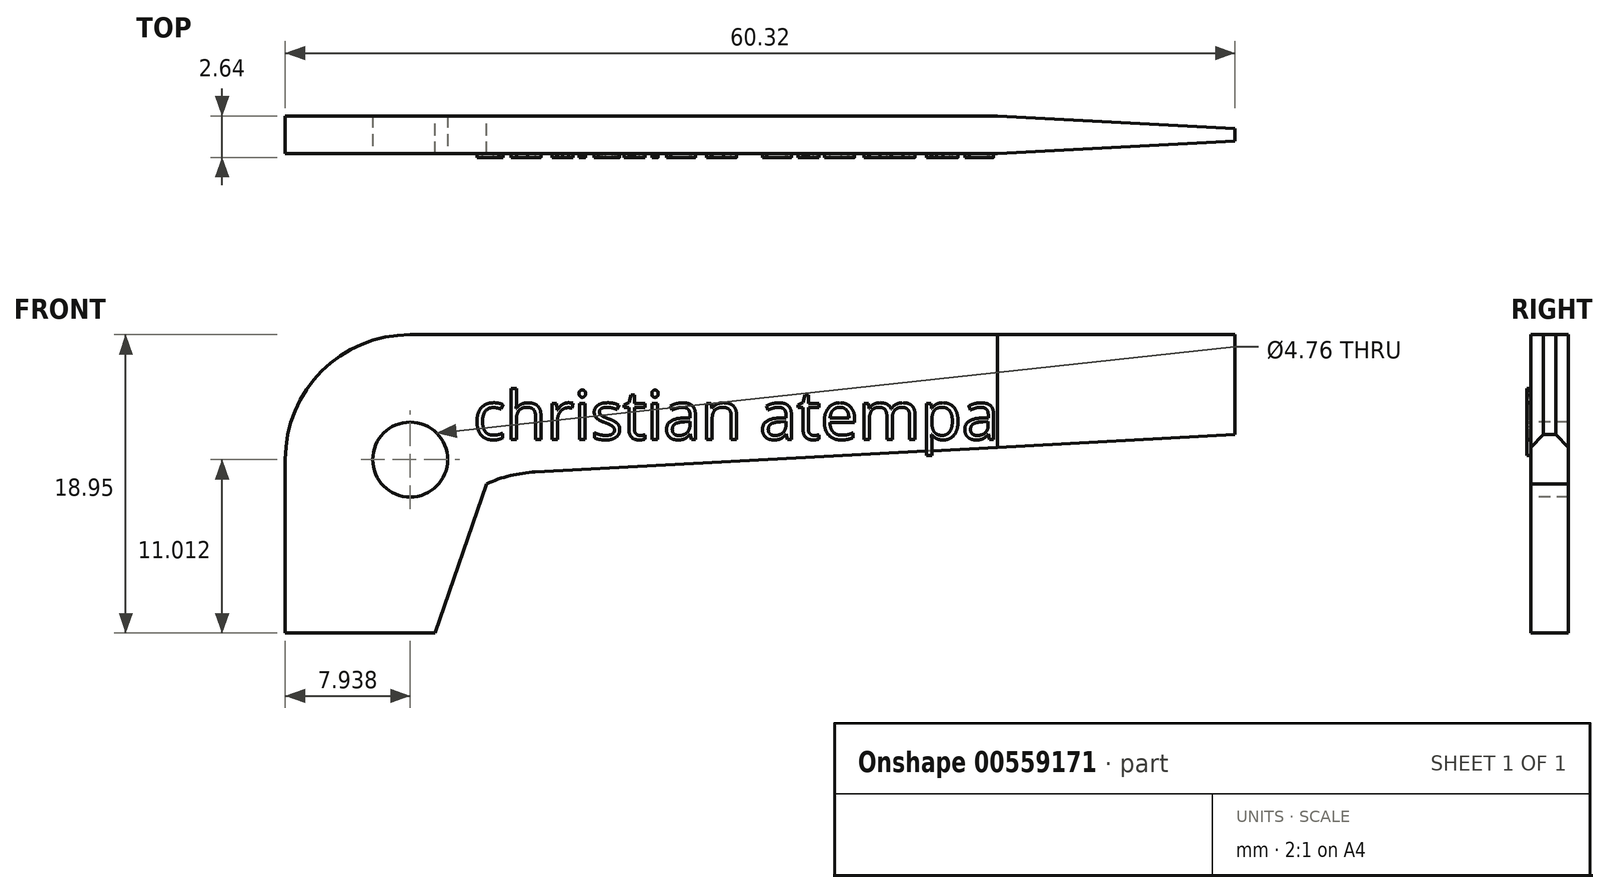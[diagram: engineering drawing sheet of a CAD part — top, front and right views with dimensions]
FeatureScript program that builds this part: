
annotation { "Feature Type Name" : "Feature", "Feature Type Description" : "" }
export const myFeature = defineFeature(function(context is Context, id is Id, definition is map)
    precondition{}
    {
        {
            var Q0;
            Q0=qCreatedBy(makeId("Front.planeOp"),FACE);
            var sketch = newSketch(context, id + "F0", { "sketchPlane" : qUnion([Q0])});
            skLineSegment(sketch, "E0.top", {"start": v(7.94, 18.95) * mm, "end": v(60.33, 18.95) * mm});
            skLineSegment(sketch, "E0.left", {"start": v(0, 0) * mm, "end": v(0, 11.01) * mm});
            skLineSegment(sketch, "E1", {"start": v(9.53, 0) * mm, "end": v(12.79, 9.47) * mm});
            skPoint(sketch, "E1.endSnap0", {"position": v(0, 9.47) * mm});
            skLineSegment(sketch, "E2", {"start": v(60.33, 12.6) * mm, "end": v(15.88, 10.22) * mm});
            skLineSegment(sketch, "E3", {"start": v(0, 0) * mm, "end": v(9.53, 0) * mm});
            skLineSegment(sketch, "E4", {"start": v(60.33, 18.95) * mm, "end": v(60.33, 12.6) * mm});
            skArc(sketch, "E5", {"start": v(15.88, 10.22) * mm, "mid": v(14.3, 10) * mm, "end": v(12.79, 9.47) * mm});
            skPoint(sketch, "E6.visualSharp", {"position": v(0, 18.95) * mm});
            skArc(sketch, "E6.filletArc", {"start": v(7.94, 18.95) * mm, "mid": v(2.32, 16.62) * mm, "end": v(0, 11.01) * mm});
            skSolve(sketch);
        }
        {
            var Q0;
            Q0 = qSketchRegion(id + "F0", true);
            extrude(context, id + "F1", {"entities" : qUnion([Q0]), "depth" : 2.38 * mm, "offsetDistance" : 25.4 * mm});
        }
        {
            var Q0;
            Q0=makeQuery(id+"F1.opExtrude","CAP_FACE",FACE,{"disambiguationData":[OSD([sQuery(id+"F0.wireOp",EDGE,"E0.top"),sQuery(id+"F0.wireOp",EDGE,"E0.left"),sQuery(id+"F0.wireOp",EDGE,"E1"),sQuery(id+"F0.wireOp",EDGE,"E2"),sQuery(id+"F0.wireOp",EDGE,"E3"),sQuery(id+"F0.wireOp",EDGE,"E4"),sQuery(id+"F0.wireOp",EDGE,"E5"),sQuery(id+"F0.wireOp",EDGE,"E6.filletArc")])],"isStart":false});
            var sketch = newSketch(context, id + "F2", { "sketchPlane" : qUnion([Q0])});
            skCircle(sketch, "E7", {"center": v(7.94, 11.01) * mm, "radius": 2.38 * mm});
            skSolve(sketch);
        }
        {
            var Q0;
            Q0=makeQuery(id+"F2.imprint","IMPRINT",FACE,{"disambiguationData":[TD([[makeQuery(id+"F2.imprint","IMPRINT",EDGE,{"derivedFrom":sQuery(id+"F2.wireOp",EDGE,"E7")}),1.0]])]});
            extrude(context, id + "F3", {"entities" : qUnion([Q0]), "operationType" : NewBodyOperationType.REMOVE, "endBound" : BoundingType.THROUGH_ALL, "oppositeDirection" : true, "depth" : 25.4 * mm, "offsetDistance" : 25.4 * mm});
        }
        {
            var Q0;
            Q0=makeQuery(id+"F1.opExtrude","SWEPT_FACE",FACE,{"disambiguationData":[OSD([sQuery(id+"F0.wireOp",EDGE,"E0.top")])]});
            var sketch = newSketch(context, id + "F4", { "sketchPlane" : qUnion([Q0])});
            skLineSegment(sketch, "E8", {"start": v(45.24, 0) * mm, "end": v(60.33, -0.8) * mm});
            skLineSegment(sketch, "E9", {"start": v(60.33, 0) * mm, "end": v(45.24, 0) * mm});
            skLineSegment(sketch, "E10.MirrorCS", {"start": v(45.24, -2.38) * mm, "end": v(60.33, -1.59) * mm});
            skLineSegment(sketch, "E11.MirrorCS", {"start": v(60.33, -2.38) * mm, "end": v(45.24, -2.38) * mm});
            skSolve(sketch);
        }
        {
            var Q0;
            {var subQ0=sQuery(id+"F4.wireOp",EDGE,"E10.MirrorCS");Q0=makeQuery(id+"F4.imprint","IMPRINT",FACE,{"disambiguationData":[TD([[makeQuery(id+"F4.imprint","IMPRINT",EDGE,{"derivedFrom":subQ0}),-1.0]])]});}
            var Q1;
            {var subQ0=sQuery(id+"F4.wireOp",EDGE,"E8");Q1=makeQuery(id+"F4.imprint","IMPRINT",FACE,{"disambiguationData":[TD([[makeQuery(id+"F4.imprint","IMPRINT",EDGE,{"derivedFrom":subQ0}),1.0]])]});}
            extrude(context, id + "F5", {"entities" : qUnion([Q0, Q1]), "operationType" : NewBodyOperationType.REMOVE, "oppositeDirection" : true, "depth" : 25.4 * mm, "offsetDistance" : 25.4 * mm});
        }
        {
            var Q0;
            Q0=makeQuery(id+"F1.opExtrude","CAP_FACE",FACE,{"disambiguationData":[OSD([sQuery(id+"F0.wireOp",EDGE,"E0.top"),sQuery(id+"F0.wireOp",EDGE,"E0.left"),sQuery(id+"F0.wireOp",EDGE,"E1"),sQuery(id+"F0.wireOp",EDGE,"E2"),sQuery(id+"F0.wireOp",EDGE,"E3"),sQuery(id+"F0.wireOp",EDGE,"E4"),sQuery(id+"F0.wireOp",EDGE,"E5"),sQuery(id+"F0.wireOp",EDGE,"E6.filletArc")])],"isStart":false});
            var sketch = newSketch(context, id + "F6", { "sketchPlane" : qUnion([Q0])});
            skText(sketch, "E12", { "text": "christian atempa", "fontName": "OpenSans-Regular.ttf"});
            const initialGuessF6  = {"E12": [0.01194, 0.0123, 1, 0, 0.00307]};
            skSetInitialGuess(sketch, initialGuessF6);
            skSolve(sketch);
        }
        {
            var Q0;
            Q0 = qSketchRegion(id + "F6", true);
            extrude(context, id + "F7", {"entities" : qUnion([Q0]), "operationType" : NewBodyOperationType.ADD, "depth" : 0.25 * mm, "offsetDistance" : 25.4 * mm});
        }
    });
